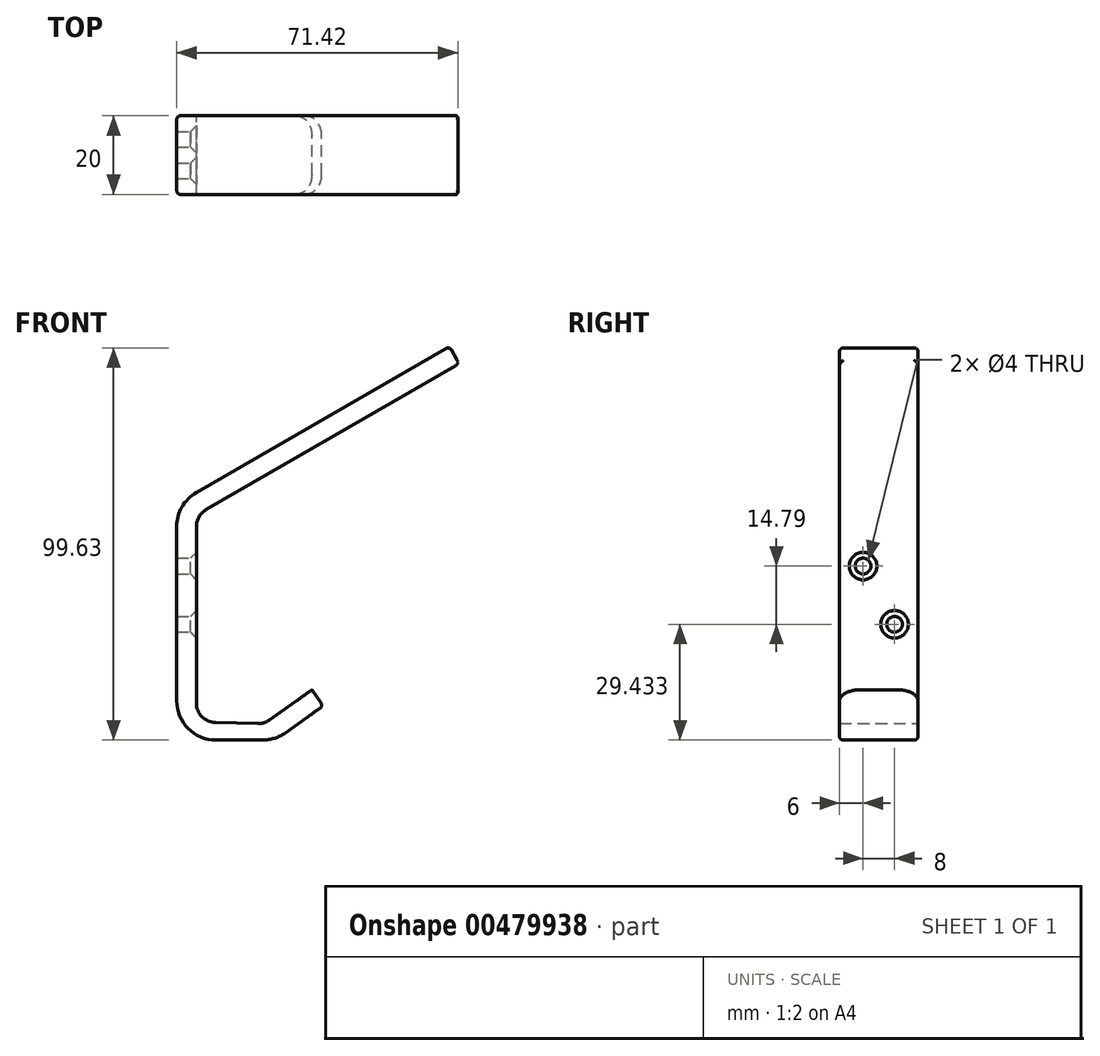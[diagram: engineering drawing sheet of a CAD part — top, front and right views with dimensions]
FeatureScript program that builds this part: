
annotation { "Feature Type Name" : "Feature", "Feature Type Description" : "" }
export const myFeature = defineFeature(function(context is Context, id is Id, definition is map)
    precondition{}
    {
        {
            var Q0;
            Q0=qCreatedBy(makeId("Front.planeOp"),FACE);
            var sketch = newSketch(context, id + "F0", { "sketchPlane" : qUnion([Q0])});
            skLineSegment(sketch, "E0", {"start": v(38.3, -46.1) * mm, "end": v(13.3, -46.1) * mm});
            skLineSegment(sketch, "E1", {"start": v(13.3, -46.1) * mm, "end": v(13.3, 13.9) * mm});
            skLineSegment(sketch, "E2", {"start": v(13.3, 13.9) * mm, "end": v(82.58, 53.9) * mm});
            skLineSegment(sketch, "E3", {"start": v(82.58, 53.9) * mm, "end": v(85.08, 49.57) * mm});
            skLineSegment(sketch, "E4", {"start": v(85.08, 49.57) * mm, "end": v(18.3, 11.01) * mm});
            skPoint(sketch, "E5.start.orphan", {"position": v(13.3, -16.1) * mm});
            skPoint(sketch, "E6.start.orphan", {"position": v(25.8, -46.1) * mm});
            skPoint(sketch, "E7.start.orphan", {"position": v(43.97, -41.14) * mm});
            skPoint(sketch, "E8.end.orphan", {"position": v(49.64, -36.18) * mm});
            skLineSegment(sketch, "E9", {"start": v(18.3, 11.01) * mm, "end": v(18.3, -41.55) * mm});
            skLineSegment(sketch, "E10", {"start": v(38.3, -46.1) * mm, "end": v(50.53, -37.43) * mm});
            skLineSegment(sketch, "E11", {"start": v(50.53, -37.43) * mm, "end": v(47.64, -33.35) * mm});
            skLineSegment(sketch, "E12", {"start": v(47.64, -33.35) * mm, "end": v(35.5, -41.96) * mm});
            skLineSegment(sketch, "E13", {"start": v(18.3, -41.55) * mm, "end": v(35.5, -41.96) * mm});
            skPoint(sketch, "E14.orphan", {"position": v(39.81, -42.07) * mm});
            skPoint(sketch, "E15.end.orphan", {"position": v(0, -46.1) * mm});
            skPoint(sketch, "E16.orphan", {"position": v(35.35, -42.07) * mm});
            skSolve(sketch);
        }
        {
            var Q0;
            Q0 = qSketchRegion(id + "F0", true);
            extrude(context, id + "F1", {"entities" : qUnion([Q0]), "depth" : 20 * mm, "offsetDistance" : 25 * mm});
        }
        {
            var Q0;
            Q0=makeQuery(id+"F1.opExtrude","SWEPT_EDGE",EDGE,{"disambiguationData":[OSD([sQuery(id+"F0.wireOp",EDGE,"E1"),sQuery(id+"F0.wireOp",EDGE,"E2")])]});
            var Q1;
            Q1=makeQuery(id+"F1.opExtrude","SWEPT_EDGE",EDGE,{"disambiguationData":[OSD([sQuery(id+"F0.wireOp",EDGE,"E0"),sQuery(id+"F0.wireOp",EDGE,"E1")])]});
            fillet(context, id + "F2", {"entities" : qUnion([Q0, Q1]), "radius" : 10 * mm, "tangentPropagation" : true, "allowEdgeOverflow" : false});
        }
        {
            var Q0;
            Q0=makeQuery(id+"F1.opExtrude","SWEPT_EDGE",EDGE,{"disambiguationData":[OSD([sQuery(id+"F0.wireOp",EDGE,"E0"),sQuery(id+"F0.wireOp",EDGE,"E10")])]});
            fillet(context, id + "F3", {"entities" : qUnion([Q0]), "radius" : 10 * mm, "tangentPropagation" : true, "allowEdgeOverflow" : false});
        }
        {
            var Q0;
            Q0=makeQuery(id+"F1.opExtrude","SWEPT_EDGE",EDGE,{"disambiguationData":[OSD([sQuery(id+"F0.wireOp",EDGE,"E4"),sQuery(id+"F0.wireOp",EDGE,"E9")])]});
            fillet(context, id + "F4", {"entities" : qUnion([Q0]), "radius" : 5 * mm, "tangentPropagation" : true, "allowEdgeOverflow" : false});
        }
        {
            var Q0;
            Q0=makeQuery(id+"F1.opExtrude","SWEPT_EDGE",EDGE,{"disambiguationData":[OSD([sQuery(id+"F0.wireOp",EDGE,"E9"),sQuery(id+"F0.wireOp",EDGE,"E13")])]});
            fillet(context, id + "F5", {"entities" : qUnion([Q0]), "radius" : 5 * mm, "tangentPropagation" : true, "allowEdgeOverflow" : false});
        }
        {
            var Q0;
            Q0=makeQuery(id+"F1.opExtrude","SWEPT_EDGE",EDGE,{"disambiguationData":[OSD([sQuery(id+"F0.wireOp",EDGE,"E12"),sQuery(id+"F0.wireOp",EDGE,"E13")])]});
            fillet(context, id + "F6", {"entities" : qUnion([Q0]), "radius" : 5 * mm, "tangentPropagation" : true, "allowEdgeOverflow" : false});
        }
        {
            var Q0;
            Q0=makeQuery(id+"F1.opExtrude","SWEPT_FACE",FACE,{"disambiguationData":[OSD([sQuery(id+"F0.wireOp",EDGE,"E9")])]});
            var sketch = newSketch(context, id + "F7", { "sketchPlane" : qUnion([Q0])});
            skPoint(sketch, "E17", {"position": v(-6, -16.67) * mm});
            skPoint(sketch, "E18", {"position": v(-14, -1.88) * mm});
            skSolve(sketch);
        }
        {
            var Q0;
            Q0=sQuery(id+"F7.wireOp",VERTEX,"E17");
            var Q1;
            Q1=sQuery(id+"F7.wireOp",VERTEX,"E18");
            var Q2;
            Q2=makeQuery(id+"F1.opExtrude","SWEPT_BODY",BODY,{"disambiguationData":[OSD([sQuery(id+"F0.wireOp",EDGE,"E0"),sQuery(id+"F0.wireOp",EDGE,"E1"),sQuery(id+"F0.wireOp",EDGE,"E2"),sQuery(id+"F0.wireOp",EDGE,"E3"),sQuery(id+"F0.wireOp",EDGE,"E4"),sQuery(id+"F0.wireOp",EDGE,"E9"),sQuery(id+"F0.wireOp",EDGE,"E10"),sQuery(id+"F0.wireOp",EDGE,"E11"),sQuery(id+"F0.wireOp",EDGE,"E12"),sQuery(id+"F0.wireOp",EDGE,"E13")])]});
            hole(context, id + "F8", {"style" : HoleStyle.C_SINK, "endStyle" : HoleEndStyle.BLIND, "holeDiameter" : 4 * mm, "cSinkDiameter" : 7 * mm, "cSinkAngle" : 90 * degree, "holeDepth" : 12 * mm, "isTappedThrough" : true, "tappedDepth" : 12 * mm, "tapClearance" : 3, "startFromSketch" : true, "locations" : qUnion([Q0, Q1]), "scope" : qUnion([Q2])});
        }
        {
            var Q0;
            Q0=makeQuery(id+"F1.opExtrude","CAP_EDGE",EDGE,{"disambiguationData":[OSD([sQuery(id+"F0.wireOp",EDGE,"E11")])],"isStart":true});
            var Q1;
            Q1=makeQuery(id+"F1.opExtrude","CAP_EDGE",EDGE,{"disambiguationData":[OSD([sQuery(id+"F0.wireOp",EDGE,"E11")])],"isStart":false});
            fillet(context, id + "F9", {"entities" : qUnion([Q0, Q1]), "radius" : 5 * mm, "tangentPropagation" : true, "allowEdgeOverflow" : false});
        }
        {
            var Q0;
            Q0=makeQuery(id+"F1.opExtrude","CAP_EDGE",EDGE,{"disambiguationData":[OSD([sQuery(id+"F0.wireOp",EDGE,"E2")])],"isStart":false});
            var Q1;
            {var subQ0=sQuery(id+"F0.wireOp",EDGE,"E2");var subQ1=sQuery(id+"F0.wireOp",EDGE,"E1");Q1=makeQuery(id+"F2.opFillet","BLEND_EDGE",EDGE,{"blendedFrom":[makeQuery(id+"F1.opExtrude","SWEPT_EDGE",EDGE,{"disambiguationData":[OSD([subQ1,subQ0])]}),makeQuery(id+"F1.opExtrude","CAP_FACE",FACE,{"disambiguationData":[OSD([sQuery(id+"F0.wireOp",EDGE,"E0"),subQ1,subQ0,sQuery(id+"F0.wireOp",EDGE,"E3"),sQuery(id+"F0.wireOp",EDGE,"E4"),sQuery(id+"F0.wireOp",EDGE,"E9"),sQuery(id+"F0.wireOp",EDGE,"E10"),sQuery(id+"F0.wireOp",EDGE,"E11"),sQuery(id+"F0.wireOp",EDGE,"E12"),sQuery(id+"F0.wireOp",EDGE,"E13")])],"isStart":false})],"blendedInto":[makeQuery(id+"F1.opExtrude","CAP_FACE",FACE,{"disambiguationData":[OSD([sQuery(id+"F0.wireOp",EDGE,"E0"),subQ1,subQ0,sQuery(id+"F0.wireOp",EDGE,"E3"),sQuery(id+"F0.wireOp",EDGE,"E4"),sQuery(id+"F0.wireOp",EDGE,"E9"),sQuery(id+"F0.wireOp",EDGE,"E10"),sQuery(id+"F0.wireOp",EDGE,"E11"),sQuery(id+"F0.wireOp",EDGE,"E12"),sQuery(id+"F0.wireOp",EDGE,"E13")])],"isStart":false})]});}
            var Q2;
            Q2=makeQuery(id+"F1.opExtrude","CAP_EDGE",EDGE,{"disambiguationData":[OSD([sQuery(id+"F0.wireOp",EDGE,"E1")])],"isStart":false});
            var Q3;
            {var subQ0=sQuery(id+"F0.wireOp",EDGE,"E1");var subQ1=sQuery(id+"F0.wireOp",EDGE,"E0");Q3=makeQuery(id+"F2.opFillet","BLEND_EDGE",EDGE,{"blendedFrom":[makeQuery(id+"F1.opExtrude","SWEPT_EDGE",EDGE,{"disambiguationData":[OSD([subQ1,subQ0])]}),makeQuery(id+"F1.opExtrude","CAP_FACE",FACE,{"disambiguationData":[OSD([subQ1,subQ0,sQuery(id+"F0.wireOp",EDGE,"E2"),sQuery(id+"F0.wireOp",EDGE,"E3"),sQuery(id+"F0.wireOp",EDGE,"E4"),sQuery(id+"F0.wireOp",EDGE,"E9"),sQuery(id+"F0.wireOp",EDGE,"E10"),sQuery(id+"F0.wireOp",EDGE,"E11"),sQuery(id+"F0.wireOp",EDGE,"E12"),sQuery(id+"F0.wireOp",EDGE,"E13")])],"isStart":false})],"blendedInto":[makeQuery(id+"F1.opExtrude","CAP_FACE",FACE,{"disambiguationData":[OSD([subQ1,subQ0,sQuery(id+"F0.wireOp",EDGE,"E2"),sQuery(id+"F0.wireOp",EDGE,"E3"),sQuery(id+"F0.wireOp",EDGE,"E4"),sQuery(id+"F0.wireOp",EDGE,"E9"),sQuery(id+"F0.wireOp",EDGE,"E10"),sQuery(id+"F0.wireOp",EDGE,"E11"),sQuery(id+"F0.wireOp",EDGE,"E12"),sQuery(id+"F0.wireOp",EDGE,"E13")])],"isStart":false})]});}
            var Q4;
            Q4=makeQuery(id+"F1.opExtrude","CAP_EDGE",EDGE,{"disambiguationData":[OSD([sQuery(id+"F0.wireOp",EDGE,"E0")])],"isStart":false});
            var Q5;
            {var subQ0=sQuery(id+"F0.wireOp",EDGE,"E10");var subQ1=sQuery(id+"F0.wireOp",EDGE,"E0");Q5=makeQuery(id+"F3.opFillet","BLEND_EDGE",EDGE,{"blendedFrom":[makeQuery(id+"F1.opExtrude","SWEPT_EDGE",EDGE,{"disambiguationData":[OSD([subQ1,subQ0])]}),makeQuery(id+"F1.opExtrude","CAP_FACE",FACE,{"disambiguationData":[OSD([subQ1,sQuery(id+"F0.wireOp",EDGE,"E1"),sQuery(id+"F0.wireOp",EDGE,"E2"),sQuery(id+"F0.wireOp",EDGE,"E3"),sQuery(id+"F0.wireOp",EDGE,"E4"),sQuery(id+"F0.wireOp",EDGE,"E9"),subQ0,sQuery(id+"F0.wireOp",EDGE,"E11"),sQuery(id+"F0.wireOp",EDGE,"E12"),sQuery(id+"F0.wireOp",EDGE,"E13")])],"isStart":false})],"blendedInto":[makeQuery(id+"F1.opExtrude","CAP_FACE",FACE,{"disambiguationData":[OSD([subQ1,sQuery(id+"F0.wireOp",EDGE,"E1"),sQuery(id+"F0.wireOp",EDGE,"E2"),sQuery(id+"F0.wireOp",EDGE,"E3"),sQuery(id+"F0.wireOp",EDGE,"E4"),sQuery(id+"F0.wireOp",EDGE,"E9"),subQ0,sQuery(id+"F0.wireOp",EDGE,"E11"),sQuery(id+"F0.wireOp",EDGE,"E12"),sQuery(id+"F0.wireOp",EDGE,"E13")])],"isStart":false})]});}
            var Q6;
            Q6=makeQuery(id+"F1.opExtrude","CAP_EDGE",EDGE,{"disambiguationData":[OSD([sQuery(id+"F0.wireOp",EDGE,"E10")])],"isStart":false});
            fillet(context, id + "F10", {"entities" : qUnion([Q0, Q1, Q2, Q3, Q4, Q5, Q6]), "radius" : 1 * mm, "tangentPropagation" : true, "allowEdgeOverflow" : false});
        }
        {
            var Q0;
            Q0=makeQuery(id+"F1.opExtrude","SWEPT_EDGE",EDGE,{"disambiguationData":[OSD([sQuery(id+"F0.wireOp",EDGE,"E3"),sQuery(id+"F0.wireOp",EDGE,"E4")])]});
            var Q1;
            Q1=makeQuery(id+"F1.opExtrude","SWEPT_EDGE",EDGE,{"disambiguationData":[OSD([sQuery(id+"F0.wireOp",EDGE,"E2"),sQuery(id+"F0.wireOp",EDGE,"E3")])]});
            fillet(context, id + "F11", {"entities" : qUnion([Q0, Q1]), "radius" : 1 * mm, "tangentPropagation" : true, "allowEdgeOverflow" : false});
        }
    });
